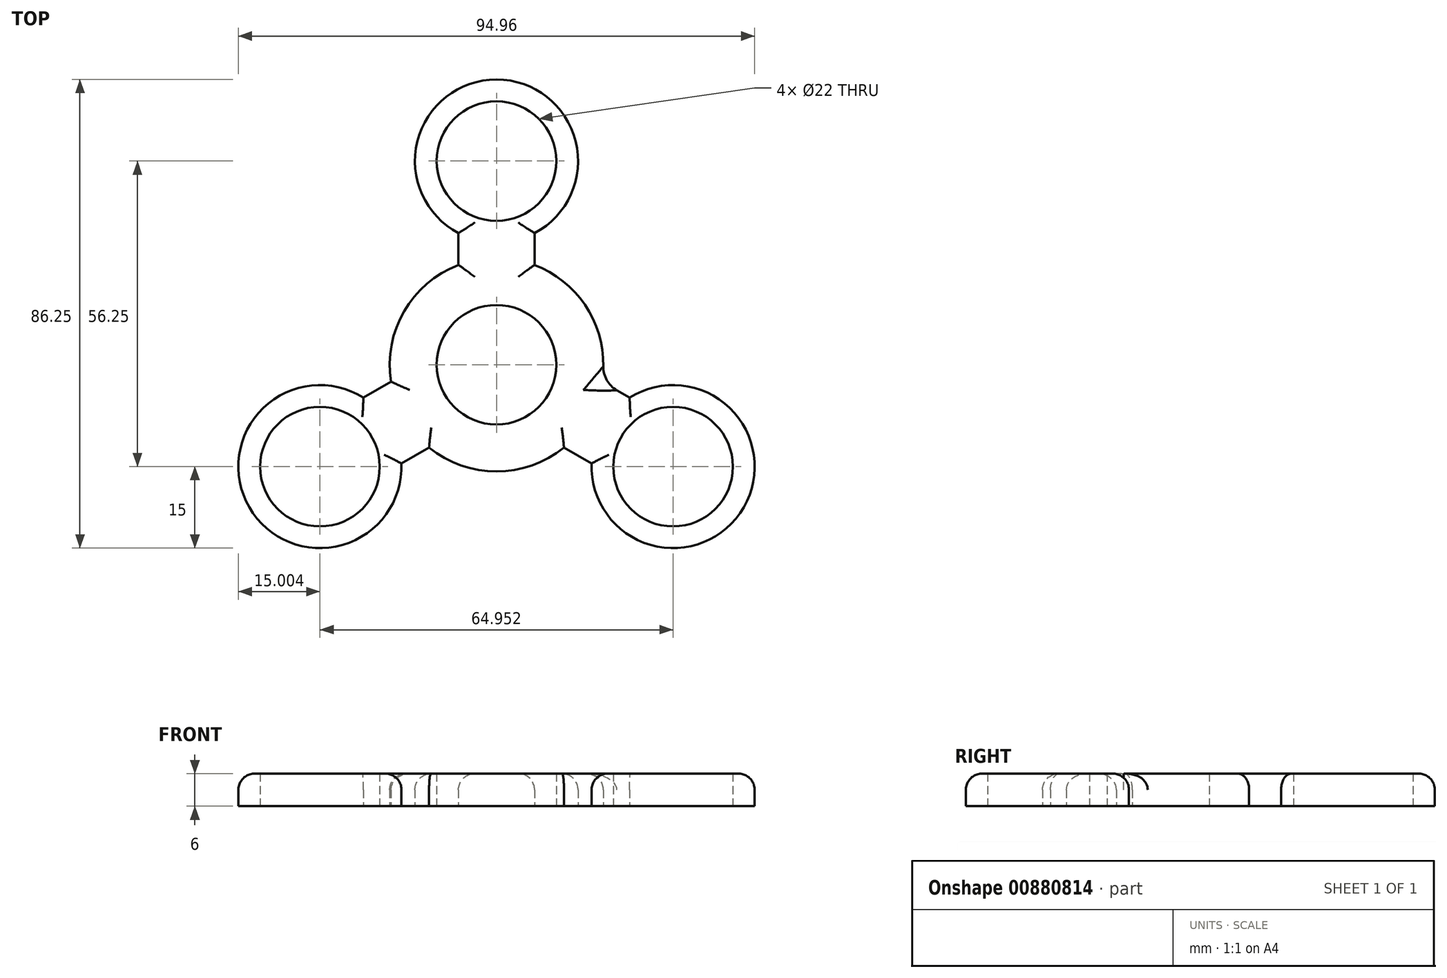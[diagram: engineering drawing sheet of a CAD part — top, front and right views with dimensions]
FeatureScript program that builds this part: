
annotation { "Feature Type Name" : "Feature", "Feature Type Description" : "" }
export const myFeature = defineFeature(function(context is Context, id is Id, definition is map)
    precondition{}
    {
        {
            var Q0;
            Q0=qCreatedBy(makeId("Top.planeOp"),FACE);
            var sketch = newSketch(context, id + "F0", { "sketchPlane" : qUnion([Q0])});
            skPoint(sketch, "E0.center", {"position": v(0, 0) * mm});
            skArc(sketch, "E1", {"start": v(7, 24.23) * mm, "mid": v(0, 52.5) * mm, "end": v(-7, 24.23) * mm});
            skArc(sketch, "E2", {"start": v(-24.49, -6.05) * mm, "mid": v(-45.47, -26.25) * mm, "end": v(-17.49, -18.18) * mm});
            skArc(sketch, "E3", {"start": v(17.49, -18.18) * mm, "mid": v(45.47, -26.25) * mm, "end": v(24.49, -6.05) * mm});
            skLineSegment(sketch, "E4.0", {"start": v(-17.49, -18.18) * mm, "end": v(-12.4, -15.24) * mm});
            skLineSegment(sketch, "E5.0", {"start": v(-24.49, -6.05) * mm, "end": v(-19.4, -3.12) * mm});
            skLineSegment(sketch, "E6.0", {"start": v(12.4, -15.24) * mm, "end": v(17.49, -18.18) * mm});
            skLineSegment(sketch, "E7.0", {"start": v(19.4, -3.12) * mm, "end": v(24.49, -6.05) * mm});
            skLineSegment(sketch, "E8.trimOffspring", {"start": v(-7, 24.23) * mm, "end": v(-7, 18.36) * mm});
            skLineSegment(sketch, "E9.trimOffspring", {"start": v(7, 24.23) * mm, "end": v(7, 18.36) * mm});
            skArc(sketch, "E10", {"start": v(-7, 18.36) * mm, "mid": v(-17.01, 9.82) * mm, "end": v(-19.4, -3.12) * mm});
            skArc(sketch, "E11.trimOffspring", {"start": v(19.4, -3.12) * mm, "mid": v(17.01, 9.82) * mm, "end": v(7, 18.36) * mm});
            skArc(sketch, "E12.trimOffspring", {"start": v(-12.4, -15.24) * mm, "mid": v(0, -19.65) * mm, "end": v(12.4, -15.24) * mm});
            skCircle(sketch, "E13", {"center": v(0, 37.5) * mm, "radius": 11 * mm});
            skCircle(sketch, "E14", {"center": v(-32.48, -18.75) * mm, "radius": 11 * mm});
            skCircle(sketch, "E15", {"center": v(32.48, -18.75) * mm, "radius": 11 * mm});
            skCircle(sketch, "E16", {"center": v(0, 0) * mm, "radius": 11 * mm});
            skSolve(sketch);
        }
        {
            var Q0;
            Q0 = qSketchRegion(id + "F0", true);
            extrude(context, id + "F1", {"entities" : qUnion([Q0]), "depth" : 6 * mm, "offsetDistance" : 25 * mm});
        }
        {
            var Q0;
            Q0=makeQuery(id+"F1.opExtrude","CAP_EDGE",EDGE,{"disambiguationData":[OSD([sQuery(id+"F0.wireOp",EDGE,"E2")])],"isStart":false});
            var Q1;
            Q1=makeQuery(id+"F1.opExtrude","CAP_EDGE",EDGE,{"disambiguationData":[OSD([sQuery(id+"F0.wireOp",EDGE,"E4.0")])],"isStart":false});
            var Q2;
            Q2=makeQuery(id+"F1.opExtrude","CAP_EDGE",EDGE,{"disambiguationData":[OSD([sQuery(id+"F0.wireOp",EDGE,"E5.0")])],"isStart":false});
            var Q3;
            Q3=makeQuery(id+"F1.opExtrude","CAP_EDGE",EDGE,{"disambiguationData":[OSD([sQuery(id+"F0.wireOp",EDGE,"E10")])],"isStart":false});
            var Q4;
            Q4=makeQuery(id+"F1.opExtrude","CAP_EDGE",EDGE,{"disambiguationData":[OSD([sQuery(id+"F0.wireOp",EDGE,"E12.trimOffspring")])],"isStart":false});
            var Q5;
            Q5=makeQuery(id+"F1.opExtrude","CAP_EDGE",EDGE,{"disambiguationData":[OSD([sQuery(id+"F0.wireOp",EDGE,"E6.0")])],"isStart":false});
            var Q6;
            Q6=makeQuery(id+"F1.opExtrude","CAP_EDGE",EDGE,{"disambiguationData":[OSD([sQuery(id+"F0.wireOp",EDGE,"E7.0")])],"isStart":false});
            var Q7;
            Q7=makeQuery(id+"F1.opExtrude","CAP_EDGE",EDGE,{"disambiguationData":[OSD([sQuery(id+"F0.wireOp",EDGE,"E3")])],"isStart":false});
            var Q8;
            Q8=makeQuery(id+"F1.opExtrude","CAP_EDGE",EDGE,{"disambiguationData":[OSD([sQuery(id+"F0.wireOp",EDGE,"E11.trimOffspring")])],"isStart":false});
            var Q9;
            Q9=makeQuery(id+"F1.opExtrude","CAP_EDGE",EDGE,{"disambiguationData":[OSD([sQuery(id+"F0.wireOp",EDGE,"E9.trimOffspring")])],"isStart":false});
            var Q10;
            Q10=makeQuery(id+"F1.opExtrude","CAP_EDGE",EDGE,{"disambiguationData":[OSD([sQuery(id+"F0.wireOp",EDGE,"E8.trimOffspring")])],"isStart":false});
            var Q11;
            Q11=makeQuery(id+"F1.opExtrude","CAP_EDGE",EDGE,{"disambiguationData":[OSD([sQuery(id+"F0.wireOp",EDGE,"E1")])],"isStart":false});
            fillet(context, id + "F2", {"entities" : qUnion([Q0, Q1, Q2, Q3, Q4, Q5, Q6, Q7, Q8, Q9, Q10, Q11]), "radius" : 3 * mm, "tangentPropagation" : true, "allowEdgeOverflow" : false});
        }
        {
            var Q0;
            Q0=makeQuery(id+"F2.opFillet","BLEND_EDGE",EDGE,{"blendedFrom":[makeQuery(id+"F1.opExtrude","CAP_EDGE",EDGE,{"disambiguationData":[OSD([sQuery(id+"F0.wireOp",EDGE,"E7.0")])],"isStart":false}),makeQuery(id+"F1.opExtrude","CAP_EDGE",EDGE,{"disambiguationData":[OSD([sQuery(id+"F0.wireOp",EDGE,"E11.trimOffspring")])],"isStart":false})],"blendedInto":[]});
            var Q1;
            Q1=makeQuery(id+"F1.opExtrude","SWEPT_EDGE",EDGE,{"disambiguationData":[OSD([sQuery(id+"F0.wireOp",EDGE,"E7.0"),sQuery(id+"F0.wireOp",EDGE,"E11.trimOffspring")])]});
            fillet(context, id + "F3", {"entities" : qUnion([Q0, Q1]), "radius" : 5 * mm, "tangentPropagation" : true, "allowEdgeOverflow" : false});
        }
    });
